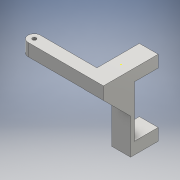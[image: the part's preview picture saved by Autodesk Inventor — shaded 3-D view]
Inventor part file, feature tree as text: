
AUTODESK INVENTOR PART (.ipt)
format: ipt  version: 2016 (Build 200138000, 138)  size: 145,920 bytes
history: native  units: mm
features: sketch x7, extrude x5, fillet x1, hole x1
ambient origin geometry x8: Origin, YZ Plane, XZ Plane, XY Plane, X Axis, Y Axis, Z Axis, Center Point
bodies: Solid1 (feature_tree)
feature tree (14):
  extrude  "Extrusion1"  Depth=60.0mm
  extrude  "Extrusion2"  Depth=41.0mm
  extrude  "Extrusion3"  Depth=10.0mm
  extrude  "Extrusion5"  Depth=15.0mm TaperAngle=0.0deg
  extrude  "Extrusion6"  Depth=15.0mm TaperAngle=0.0deg
  sketch  "Sketch7"  dims[d19=50.0mm d20=0.0mm d21=5.0mm]
  fillet  "Fillet1"  Radius=9.871mm
  hole  "Hole1"  [1 undecoded]
  sketch  "Sketch1"  dims[d0=15.0mm d1=60.0mm]
  sketch  "Sketch2"  dims[d2=3.0mm d3=0.0mm d4=41.0mm]
  sketch  "Sketch3"  dims[d5=19.0mm d6=0.0mm d7=10.0mm]
  sketch  "Sketch5"  dims[d8=21.64mm d9=15.0mm d10=0.0mm]
  sketch  "Sketch6"  dims[d15=45.0deg d16=15.0mm d17=0.0mm d18=9.871mm]
  sketch  "Sketch8"  dims[d22=3.0mm d23=6.0mm d24=4.0mm d25=2.0mm d26=90.0deg d27=8.0mm d28=20.594885mm]
note: 1 required parameter value undecoded (feature->parameter linkage not recoverable at this tier; creation-order binding heuristic only, values carry confidence <= 0.55)
